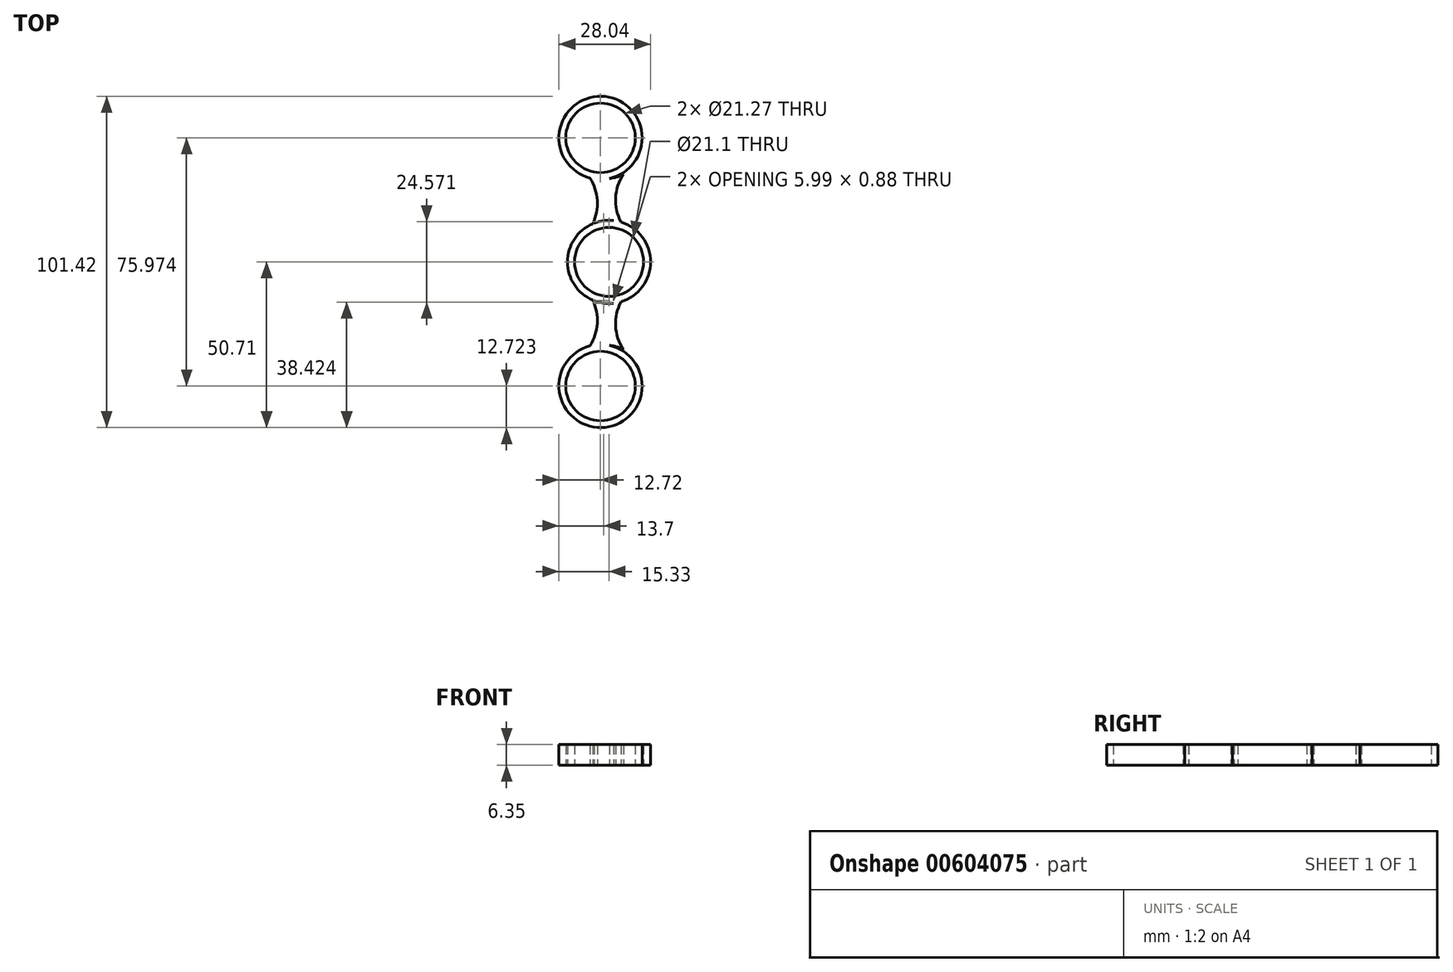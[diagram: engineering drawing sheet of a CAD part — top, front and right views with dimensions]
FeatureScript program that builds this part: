
annotation { "Feature Type Name" : "Feature", "Feature Type Description" : "" }
export const myFeature = defineFeature(function(context is Context, id is Id, definition is map)
    precondition{}
    {
        {
            var Q0;
            Q0=qCreatedBy(makeId("Top.planeOp"),FACE);
            var sketch = newSketch(context, id + "F0", { "sketchPlane" : qUnion([Q0])});
            skCircle(sketch, "E0", {"center": v(0, 0) * mm, "radius": 10.55 * mm});
            skCircle(sketch, "E1", {"center": v(0, 0) * mm, "radius": 12.71 * mm});
            skSolve(sketch);
        }
        {
            var Q0;
            Q0 = qSketchRegion(id + "F0", true);
            extrude(context, id + "F1", {"entities" : qUnion([Q0]), "depth" : 6.35 * mm, "offsetDistance" : 25.4 * mm});
        }
        {
            var Q0;
            Q0=qCreatedBy(makeId("Top.planeOp"),FACE);
            var sketch = newSketch(context, id + "F2", { "sketchPlane" : qUnion([Q0])});
            skArc(sketch, "E2", {"start": v(3.69, -12.13) * mm, "mid": v(2, -19.6) * mm, "end": v(4.44, -26.84) * mm});
            skArc(sketch, "E3", {"start": v(-6.69, -26.84) * mm, "mid": v(-3.67, -19.5) * mm, "end": v(-5, -11.69) * mm});
            skArc(sketch, "E4", {"start": v(-5, -11.69) * mm, "mid": v(-0.7, -12.71) * mm, "end": v(3.69, -12.13) * mm});
            skArc(sketch, "E5", {"start": v(4.44, -26.84) * mm, "mid": v(-1.12, -25.5) * mm, "end": v(-6.69, -26.84) * mm});
            skSolve(sketch);
        }
        {
            var Q0;
            Q0 = qSketchRegion(id + "F2", true);
            extrude(context, id + "F3", {"entities" : qUnion([Q0]), "operationType" : NewBodyOperationType.ADD, "depth" : 6.35 * mm, "offsetDistance" : 25.4 * mm});
        }
        {
            var Q0;
            Q0=qCreatedBy(makeId("Top.planeOp"),FACE);
            var sketch = newSketch(context, id + "F4", { "sketchPlane" : qUnion([Q0])});
            skCircle(sketch, "E6", {"center": v(-2.6, -37.99) * mm, "radius": 12.72 * mm});
            skCircle(sketch, "E7", {"center": v(-2.6, -37.99) * mm, "radius": 10.63 * mm});
            skSolve(sketch);
        }
        {
            var Q0;
            Q0 = qSketchRegion(id + "F4", true);
            extrude(context, id + "F5", {"entities" : qUnion([Q0]), "operationType" : NewBodyOperationType.ADD, "depth" : 6.35 * mm, "offsetDistance" : 25.4 * mm});
        }
        {
            var Q0;
            Q0=makeQuery(id+"F1.opExtrude","SWEPT_BODY",BODY,{"disambiguationData":[OSD([sQuery(id+"F0.wireOp",EDGE,"E0"),sQuery(id+"F0.wireOp",EDGE,"E1")])]});
            var Q1;
            Q1=qCreatedBy(makeId("Front.planeOp"),FACE);
            mirror(context, id + "F6", {"operationType" : NewBodyOperationType.ADD, "entities" : qUnion([Q0]), "mirrorPlane" : qUnion([Q1])});
        }
    });
